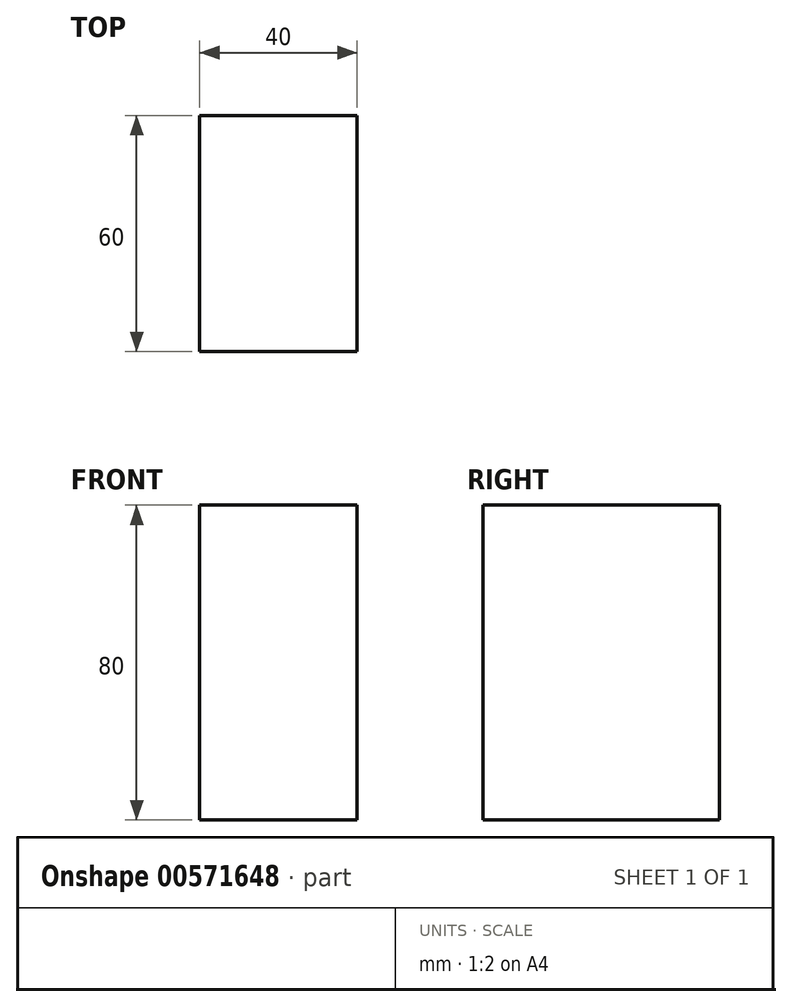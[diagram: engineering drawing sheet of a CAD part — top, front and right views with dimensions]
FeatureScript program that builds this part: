
annotation { "Feature Type Name" : "Feature", "Feature Type Description" : "" }
export const myFeature = defineFeature(function(context is Context, id is Id, definition is map)
    precondition{}
    {
        {
            var Q0;
            Q0=qCreatedBy(makeId("Top.planeOp"),FACE);
            var sketch = newSketch(context, id + "F0", { "sketchPlane" : qUnion([Q0])});
            skLineSegment(sketch, "E0.bottom", {"start": v(-0.8, -0.5) * mm, "end": v(39.2, -0.5) * mm});
            skLineSegment(sketch, "E0.top", {"start": v(-0.8, 59.5) * mm, "end": v(39.2, 59.5) * mm});
            skLineSegment(sketch, "E0.left", {"start": v(-0.8, -0.5) * mm, "end": v(-0.8, 59.5) * mm});
            skLineSegment(sketch, "E0.right", {"start": v(39.2, -0.5) * mm, "end": v(39.2, 59.5) * mm});
            skSolve(sketch);
        }
        {
            var Q0;
            Q0=makeQuery(id+"F0.imprint","IMPRINT",FACE,{"disambiguationData":[TD([[makeQuery(id+"F0.imprint","IMPRINT",EDGE,{"derivedFrom":sQuery(id+"F0.wireOp",EDGE,"E0.bottom")}),1.0]])]});
            extrude(context, id + "F1", {"entities" : qUnion([Q0]), "depth" : 80 * mm, "offsetDistance" : 25 * mm});
        }
    });
